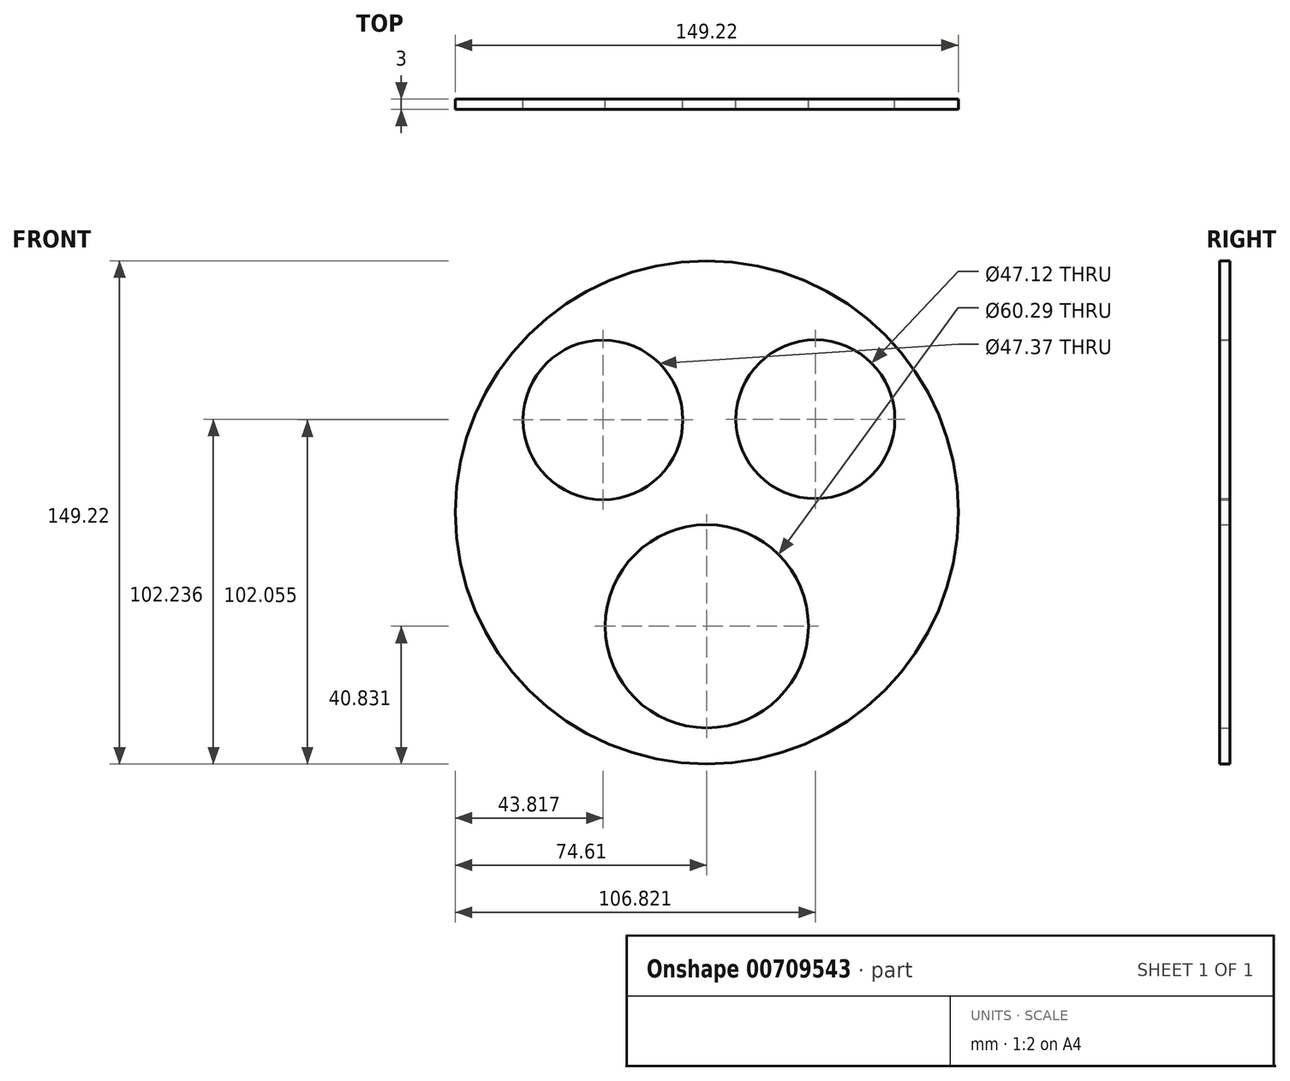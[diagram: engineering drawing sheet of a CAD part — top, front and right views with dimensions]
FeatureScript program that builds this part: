
annotation { "Feature Type Name" : "Feature", "Feature Type Description" : "" }
export const myFeature = defineFeature(function(context is Context, id is Id, definition is map)
    precondition{}
    {
        {
            var Q0;
            Q0=qCreatedBy(makeId("Front.planeOp"),FACE);
            var sketch = newSketch(context, id + "F0", { "sketchPlane" : qUnion([Q0])});
            skCircle(sketch, "E0", {"center": v(0, 0) * mm, "radius": 74.61 * mm});
            skCircle(sketch, "E1", {"center": v(32.21, 27.63) * mm, "radius": 23.56 * mm});
            skCircle(sketch, "E2", {"center": v(0, -33.78) * mm, "radius": 30.14 * mm});
            skCircle(sketch, "E3", {"center": v(-30.8, 27.44) * mm, "radius": 23.68 * mm});
            skSolve(sketch);
        }
        {
            var Q0;
            Q0 = qSketchRegion(id + "F0", true);
            extrude(context, id + "F1", {"entities" : qUnion([Q0]), "depth" : 3 * mm, "offsetDistance" : 25.4 * mm});
        }
    });
